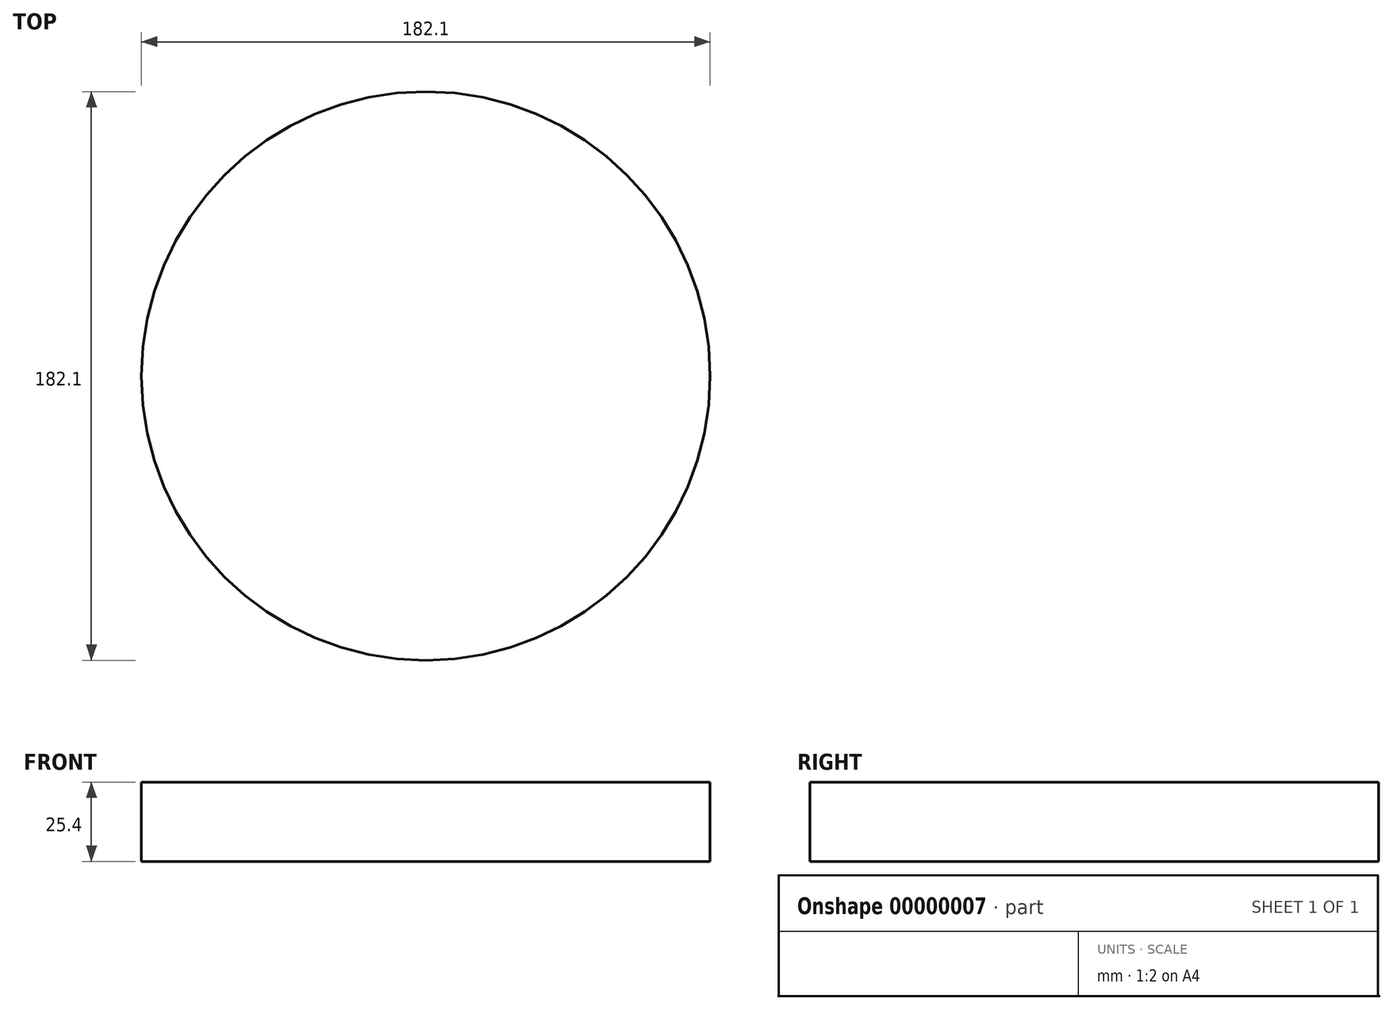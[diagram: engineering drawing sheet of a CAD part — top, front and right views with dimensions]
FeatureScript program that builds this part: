
annotation { "Feature Type Name" : "Feature", "Feature Type Description" : "" }
export const myFeature = defineFeature(function(context is Context, id is Id, definition is map)
    precondition{}
    {
        {
            var Q0;
            Q0 = qCreatedBy(makeId("Top.planeOp"), FACE);
            var sketch = newSketch(context, id + "F0", { "sketchPlane" : qUnion([Q0])});
            skCircle(sketch, "E0", {"center": v(0, 0) * mm, "radius": 91.05 * mm});
            skSolve(sketch);
        }
        {
            var Q0;
            Q0=makeQuery(id+"F0.imprint","IMPRINT",FACE,{"disambiguationData":[TD([[makeQuery(id+"F0.imprint","IMPRINT",EDGE,{"derivedFrom":sQuery(id+"F0.wireOp",EDGE,"E0")}),1.0]])]});
            extrude(context, id + "F1", {"entities" : qUnion([Q0]), "depth" : 25.4 * mm});
        }
    });
